# Revit family: JC KONTAKTER JCK218 Armbågskontakt
name_source: partatom
category: Specialty Equipment
units: mm (PartAtom-declared; Revit-internal decimal feet)

## family parameters
Always vertical = Yes
Cut with Voids When Loaded = No
Enable Cutting in Views = Yes
Host = Wall
Maintain Annotation Orientation = No
Part Type = Normal
Room Calculation Point = No
Round Connector Dimension = Use Diameter
Shared = No

## types (1)
- Armbågskontakt JCK218
    Antal mikrobrytare = 1
    CE Dokument = https://jckontakter.se
    Core Finish = Aluminum ENAW 6060
    Default Elevation = 0 mm  [stored 0 ft]
    Description = JCK218 tillhör en serie armbågskontakter som har en plan tryckyta med fyra taktila rillor i. Rillorna fungerar som extra vägledning för personer med synnedsättning. Man kan enkelt känna sig till vart man ska trycka för att aktivera dörröppning. JCK218 är tillverkad i vitlackad aluminium och har vita endcaps. Den levereras med 1st mikrobrytare i IP67, men går även att beställa med fler.
    End Cap Finish = POM Tenac C 4520 (Vit)
    Lid Finish = Aluminum ENAW 6060 (Vit)
    Längsta märkström = 1mA/4 V DC
    Manufacturer = JC Kontakter
    Microbrytare = Standard NO IP67
    Model = JCK218
    Nominell märkström = 12 V - Resistive 6A Inductive L/R 5ms 6A, 24 V - Resistive 6A Inductive L/R 5ms 5A
    Placering information = https://jckontakter.se
    Produktvikt = 0.305 kg
    Teknisk produktblad = https://jckontakter.se
    Tillvalsförteckning = https://jckontakter.se
    Tillverkarens land = Sverige
    URL = https://jckontakter.se

note: [stored X ft] marks values corroborated as IEEE doubles in the binary element streams (Revit-internal decimal feet)

## geometry (parser evidence)
native form markers: Sweep x10
no freeform markers — native parametric forms only
